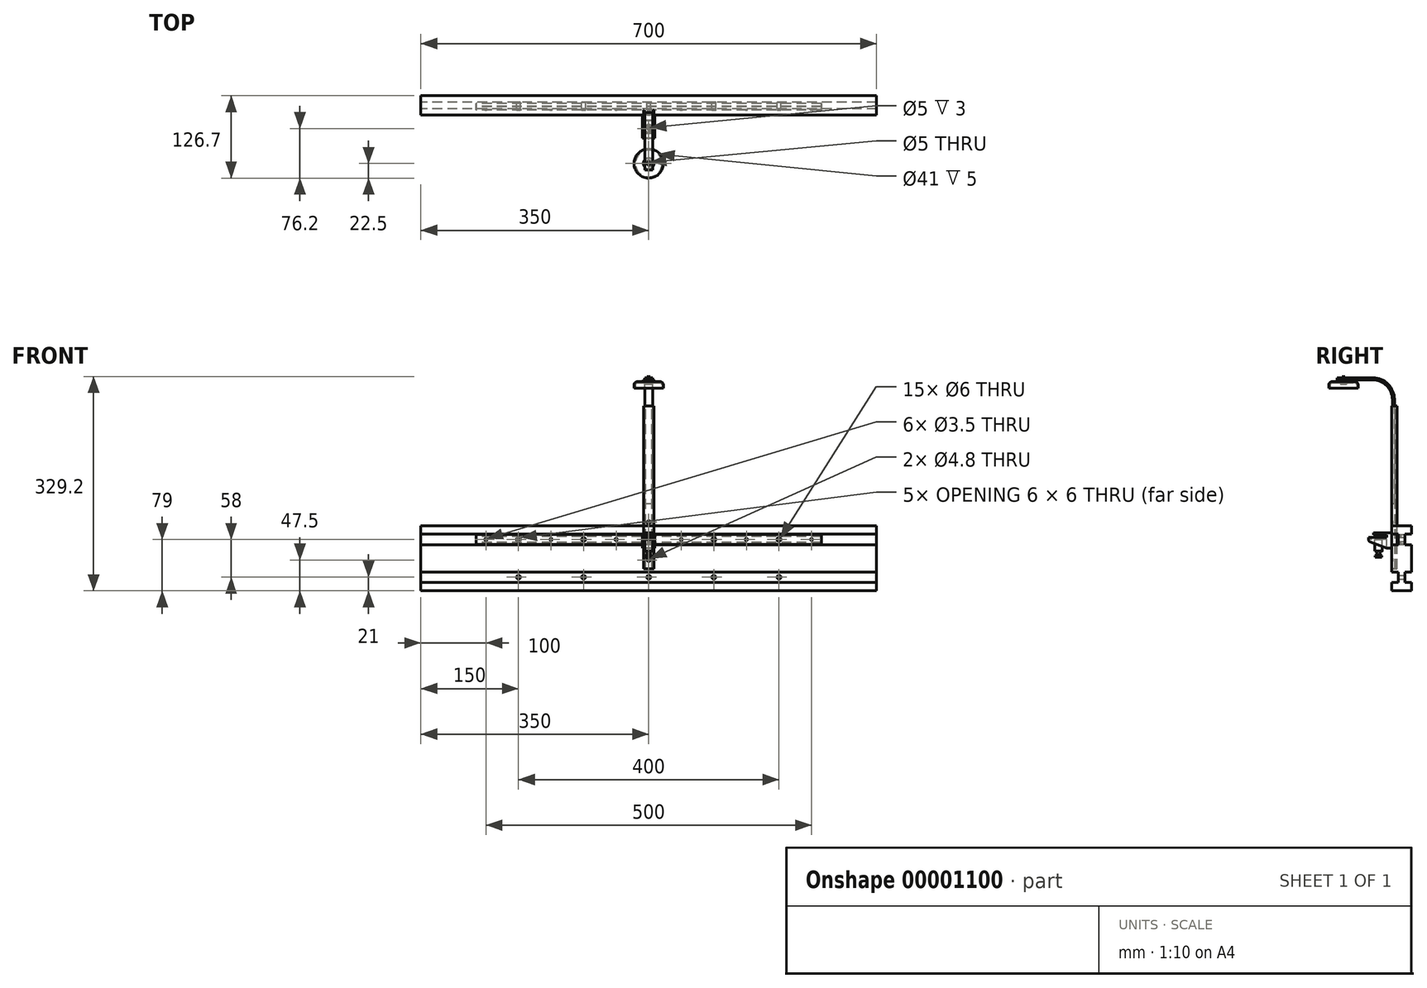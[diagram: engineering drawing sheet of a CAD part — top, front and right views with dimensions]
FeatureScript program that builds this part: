
annotation { "Feature Type Name" : "Feature", "Feature Type Description" : "" }
export const myFeature = defineFeature(function(context is Context, id is Id, definition is map)
    precondition{}
    {
        {
            var Q0;
            Q0=qCreatedBy(makeId("Right.planeOp"),FACE);
            var sketch = newSketch(context, id + "F0", { "sketchPlane" : qUnion([Q0])});
            skLineSegment(sketch, "E0", {"start": v(0, 10) * mm, "end": v(-28, 10) * mm});
            skLineSegment(sketch, "E1", {"start": v(-28, 10) * mm, "end": v(-28, 7) * mm});
            skLineSegment(sketch, "E2", {"start": v(-28, 7) * mm, "end": v(-8, 7) * mm});
            skLineSegment(sketch, "E3", {"start": v(-8, 7) * mm, "end": v(-8, 3) * mm});
            skLineSegment(sketch, "E4", {"start": v(-8, 3) * mm, "end": v(-35.5, 3) * mm});
            skLineSegment(sketch, "E5", {"start": v(-35.5, 3) * mm, "end": v(-35.5, -0.9) * mm});
            skLineSegment(sketch, "E6", {"start": v(-33.53, -3.72) * mm, "end": v(-8, -13) * mm});
            skLineSegment(sketch, "E7", {"start": v(-8, -13) * mm, "end": v(0, -13) * mm});
            skLineSegment(sketch, "E8", {"start": v(0, -13) * mm, "end": v(0, 10) * mm});
            skLineSegment(sketch, "E9", {"start": v(-8, 0) * mm, "end": v(-35.5, 0) * mm});
            skLineSegment(sketch, "E10", {"start": v(-8, -13) * mm, "end": v(-8, 0) * mm});
            skPoint(sketch, "E11.visualSharp", {"position": v(-35.5, -3) * mm});
            skArc(sketch, "E11.filletArc", {"start": v(-35.5, -0.9) * mm, "mid": v(-34.96, -2.62) * mm, "end": v(-33.53, -3.72) * mm});
            skSolve(sketch);
        }
        {
            var Q0;
            Q0 = qSketchRegion(id + "F0", true);
            extrude(context, id + "F1", {"entities" : qUnion([Q0]), "depth" : 19 * mm, "symmetric" : true});
        }
        {
            var Q0;
            {var subQ0=sQuery(id+"F0.wireOp",EDGE,"E6");Q0=makeQuery(id+"F0.imprint","IMPRINT",FACE,{"disambiguationData":[TD([[makeQuery(id+"F0.imprint","IMPRINT",EDGE,{"derivedFrom":subQ0}),1.0]])]});}
            extrude(context, id + "F2", {"entities" : qUnion([Q0]), "operationType" : NewBodyOperationType.REMOVE, "oppositeDirection" : true, "depth" : 15 * mm, "symmetric" : true});
        }
        {
            var Q0;
            Q0=qCreatedBy(makeId("Right.planeOp"),FACE);
            var sketch = newSketch(context, id + "F3", { "sketchPlane" : qUnion([Q0])});
            skLineSegment(sketch, "E12", {"start": v(-20.5, 6) * mm, "end": v(-20.5, -27) * mm});
            skLineSegment(sketch, "E13", {"start": v(-20.5, -27) * mm, "end": v(-15.5, -27) * mm});
            skLineSegment(sketch, "E14", {"start": v(-15.5, -27) * mm, "end": v(-15.5, -25) * mm});
            skLineSegment(sketch, "E15", {"start": v(-15.5, -25) * mm, "end": v(-18.25, -23.5) * mm});
            skLineSegment(sketch, "E16", {"start": v(-18.25, -23.5) * mm, "end": v(-18.25, -18) * mm});
            skLineSegment(sketch, "E17", {"start": v(-18.25, 6) * mm, "end": v(-20.5, 6) * mm});
            skLineSegment(sketch, "E18", {"start": v(-18.25, -18) * mm, "end": v(-14.5, -18) * mm});
            skLineSegment(sketch, "E19", {"start": v(-14.5, -18) * mm, "end": v(-14.5, 0) * mm});
            skLineSegment(sketch, "E20", {"start": v(-14.5, 0) * mm, "end": v(-18.25, 0) * mm});
            skLineSegment(sketch, "E21", {"start": v(-18, 0) * mm, "end": v(-18, 3) * mm});
            skLineSegment(sketch, "E22", {"start": v(-18, 3) * mm, "end": v(-18.25, 3) * mm});
            skLineSegment(sketch, "E23.trimOffspring", {"start": v(-18.25, 0) * mm, "end": v(-18.25, 6) * mm});
            skSolve(sketch);
        }
        {
            var Q0;
            {var subQ5=sQuery(id+"F3.wireOp",EDGE,"E21");Q0=makeQuery(id+"F3.imprint","IMPRINT",FACE,{"disambiguationData":[TD([[makeQuery(id+"F3.imprint","IMPRINT",EDGE,{"derivedFrom":subQ5}),1.0]])]});}
            var Q1;
            Q1=sQuery(id+"F3.wireOp",EDGE,"E12");
            revolve(context, id + "F4", {"operationType" : NewBodyOperationType.REMOVE, "entities" : qUnion([Q0]), "axis" : qUnion([Q1]), "revolveType" : RevolveType.FULL, "oppositeDirection" : true});
        }
        {
            var Q0;
            Q0=makeQuery(id+"F3.imprint","IMPRINT",FACE,{"disambiguationData":[TD([[makeQuery(id+"F3.imprint","IMPRINT",EDGE,{"derivedFrom":sQuery(id+"F3.wireOp",EDGE,"E12")}),1.0]])]});
            var Q1;
            Q1=sQuery(id+"F3.wireOp",EDGE,"E12");
            revolve(context, id + "F5", {"operationType" : NewBodyOperationType.ADD, "entities" : qUnion([Q0]), "axis" : qUnion([Q1]), "revolveType" : RevolveType.FULL});
        }
        {
            var Q0;
            Q0=makeQuery(id+"F5.opRevolve","SWEPT_EDGE",EDGE,{"disambiguationData":[OSD([sQuery(id+"F3.wireOp",EDGE,"E17"),sQuery(id+"F3.wireOp",EDGE,"E23.trimOffspring")])]});
            chamfer(context, id + "F6", {"entities" : qUnion([Q0]), "width" : .5 * mm, "tangentPropagation" : true});
        }
        {
            var Q0;
            Q0=qCreatedBy(makeId("Top.planeOp"),FACE);
            var sketch = newSketch(context, id + "F7", { "sketchPlane" : qUnion([Q0])});
            skLineSegment(sketch, "E24", {"start": v(0, 0) * mm, "end": v(-7.75, 0) * mm});
            skLineSegment(sketch, "E25", {"start": v(-7.75, 0) * mm, "end": v(-7.75, 7.8) * mm});
            skLineSegment(sketch, "E26", {"start": v(-7.75, 7.8) * mm, "end": v(-6.95, 7.8) * mm});
            skLineSegment(sketch, "E27", {"start": v(-6.95, 7.8) * mm, "end": v(-6.95, 6) * mm});
            skLineSegment(sketch, "E28", {"start": v(-6.95, 6) * mm, "end": v(-4.7, 6) * mm});
            skLineSegment(sketch, "E29", {"start": v(-4.7, 6) * mm, "end": v(-4.7, 5.2) * mm});
            skLineSegment(sketch, "E30", {"start": v(-4.7, 5.2) * mm, "end": v(-6.95, 5.2) * mm});
            skLineSegment(sketch, "E31", {"start": v(-6.95, 5.2) * mm, "end": v(-6.95, 0.8) * mm});
            skLineSegment(sketch, "E32", {"start": v(-6.95, 0.8) * mm, "end": v(0, 0.8) * mm});
            skLineSegment(sketch, "E33", {"start": v(0, 0.8) * mm, "end": v(0, 0) * mm, "construction": true});
            skLineSegment(sketch, "E34.MirrorCS", {"start": v(6.95, 0.8) * mm, "end": v(0, 0.8) * mm});
            skLineSegment(sketch, "E35.MirrorCS", {"start": v(6.95, 5.2) * mm, "end": v(6.95, 0.8) * mm});
            skLineSegment(sketch, "E36.MirrorCS", {"start": v(4.7, 5.2) * mm, "end": v(6.95, 5.2) * mm});
            skLineSegment(sketch, "E37.MirrorCS", {"start": v(4.7, 6) * mm, "end": v(4.7, 5.2) * mm});
            skLineSegment(sketch, "E38.MirrorCS", {"start": v(6.95, 6) * mm, "end": v(4.7, 6) * mm});
            skLineSegment(sketch, "E39.MirrorCS", {"start": v(6.95, 7.8) * mm, "end": v(6.95, 6) * mm});
            skLineSegment(sketch, "E40.MirrorCS", {"start": v(7.75, 7.8) * mm, "end": v(6.95, 7.8) * mm});
            skLineSegment(sketch, "E41.MirrorCS", {"start": v(7.75, 0) * mm, "end": v(7.75, 7.8) * mm});
            skLineSegment(sketch, "E42.MirrorCS", {"start": v(0, 0) * mm, "end": v(7.75, 0) * mm});
            skSolve(sketch);
        }
        {
            var Q0;
            Q0 = qSketchRegion(id + "F7", true);
            extrude(context, id + "F8", {"entities" : qUnion([Q0]), "operationType" : NewBodyOperationType.ADD, "oppositeDirection" : true, "depth" : (13 + 32) * mm, "hasSecondDirection" : true, "secondDirectionOppositeDirection" : false, "secondDirectionDepth" : (250 - 45) * mm});
        }
        {
            var Q0;
            Q0=qCreatedBy(makeId("Front.planeOp"),FACE);
            var sketch = newSketch(context, id + "F9", { "sketchPlane" : qUnion([Q0])});
            skPoint(sketch, "E43", {"position": v(0, 26.5) * mm});
            skPoint(sketch, "E44", {"position": v(0, -31.5) * mm});
            skSolve(sketch);
        }
        {
            var Q0;
            Q0=sQuery(id+"F9.wireOp",VERTEX,"E43");
            var Q1;
            Q1=sQuery(id+"F9.wireOp",VERTEX,"E44");
            var Q2;
            Q2=makeQuery(id+"F4.boolean.opBoolean","SPLIT",BODY,{"disambiguationData":[OD(0.0)],"derivedFrom":makeQuery(id+"F1.opExtrude","SWEPT_BODY",BODY,{"disambiguationData":[OSD([sQuery(id+"F0.wireOp",EDGE,"E0"),sQuery(id+"F0.wireOp",EDGE,"E1"),sQuery(id+"F0.wireOp",EDGE,"E2"),sQuery(id+"F0.wireOp",EDGE,"E3"),sQuery(id+"F0.wireOp",EDGE,"E4"),sQuery(id+"F0.wireOp",EDGE,"E5"),sQuery(id+"F0.wireOp",EDGE,"E6"),sQuery(id+"F0.wireOp",EDGE,"E7"),sQuery(id+"F0.wireOp",EDGE,"E8"),sQuery(id+"F0.wireOp",EDGE,"E11.filletArc")])]})});
            hole(context, id + "F10", {"style" : HoleStyle.SIMPLE, "endStyle" : HoleEndStyle.THROUGH, "holeDiameter" : 4.8 * mm, "locations" : qUnion([Q0, Q1]), "scope" : qUnion([Q2]), "isTappedThrough" : true});
        }
        {
            var Q0;
            Q0=qCreatedBy(makeId("Right.planeOp"),FACE);
            var sketch = newSketch(context, id + "F11", { "sketchPlane" : qUnion([Q0])});
            skLineSegment(sketch, "E45", {"start": v(0.8, 55) * mm, "end": v(0.8, 215) * mm});
            skArc(sketch, "E46", {"start": v(0.8, 215) * mm, "mid": v(-7.99, 236.21) * mm, "end": v(-29.2, 245) * mm});
            skLineSegment(sketch, "E47", {"start": v(-29.2, 245) * mm, "end": v(-84.2, 245) * mm});
            skSolve(sketch);
        }
        {
            var Q0;
            Q0=sQuery(id+"F11.wireOp",VERTEX,"E45.start");
            var Q1;
            Q1=qCreatedBy(makeId("Top.planeOp"),FACE);
            cPlane(context, id + "F12", {"entities" : qUnion([Q0, Q1]), "cplaneType" : CPlaneType.PLANE_POINT, "offset" : 25 * mm, "width" : 150 * mm, "height" : 150 * mm});
        }
        {
            var Q0;
            Q0=qCreatedBy(id+"F12.planeOp",FACE);
            var sketch = newSketch(context, id + "F13", { "sketchPlane" : qUnion([Q0])});
            skLineSegment(sketch, "E48.bottom", {"start": v(-6.15, 0.8) * mm, "end": v(6.15, 0.8) * mm});
            skLineSegment(sketch, "E48.top", {"start": v(-6.15, 4) * mm, "end": v(6.15, 4) * mm});
            skLineSegment(sketch, "E48.left", {"start": v(-6.15, 0.8) * mm, "end": v(-6.15, 4) * mm});
            skLineSegment(sketch, "E48.right", {"start": v(6.15, 0.8) * mm, "end": v(6.15, 4) * mm});
            skPoint(sketch, "E49", {"position": v(0, 0.8) * mm});
            skSolve(sketch);
        }
        {
            var Q0;
            Q0 = qSketchRegion(id + "F13", true);
            var Q1;
            Q1 = qConstructionFilter(qBodyType(qCreatedBy(id + "F11" ,EDGE), BodyType.WIRE), ConstructionObject.NO);
            sweep(context, id + "F14", {"profiles" : qUnion([Q0]), "path" : qUnion([Q1])});
        }
        {
            var Q0;
            Q0=qCreatedBy(makeId("Right.planeOp"),FACE);
            var sketch = newSketch(context, id + "F15", { "sketchPlane" : qUnion([Q0])});
            skLineSegment(sketch, "E50", {"start": v(-74.2, 250.2) * mm, "end": v(-71.7, 250.2) * mm});
            skLineSegment(sketch, "E51", {"start": v(-71.7, 250.2) * mm, "end": v(-71.7, 240.5) * mm});
            skLineSegment(sketch, "E52", {"start": v(-69.2, 240.5) * mm, "end": v(-69.2, 238.5) * mm});
            skLineSegment(sketch, "E53", {"start": v(-69.2, 238.5) * mm, "end": v(-74.2, 238.5) * mm});
            skLineSegment(sketch, "E54", {"start": v(-74.2, 238.5) * mm, "end": v(-74.2, 250.2) * mm});
            skLineSegment(sketch, "E55", {"start": v(-71.7, 245) * mm, "end": v(-65.95, 245) * mm});
            skLineSegment(sketch, "E56", {"start": v(-65.95, 245) * mm, "end": v(-65.95, 242.5) * mm});
            skLineSegment(sketch, "E57", {"start": v(-65.95, 242.5) * mm, "end": v(-56.7, 242.5) * mm});
            skLineSegment(sketch, "E58", {"start": v(-51.7, 237.5) * mm, "end": v(-51.7, 232.5) * mm});
            skLineSegment(sketch, "E59", {"start": v(-51.7, 232.5) * mm, "end": v(-53.7, 232.5) * mm});
            skLineSegment(sketch, "E60", {"start": v(-53.7, 232.5) * mm, "end": v(-53.7, 237.5) * mm});
            skLineSegment(sketch, "E61", {"start": v(-56.7, 240.5) * mm, "end": v(-71.7, 240.5) * mm});
            skPoint(sketch, "E62.visualSharp", {"position": v(-51.7, 242.5) * mm});
            skArc(sketch, "E62.filletArc", {"start": v(-51.7, 237.5) * mm, "mid": v(-53.16, 241.04) * mm, "end": v(-56.7, 242.5) * mm});
            skPoint(sketch, "E63.visualSharp", {"position": v(-53.7, 240.5) * mm});
            skArc(sketch, "E63.filletArc", {"start": v(-53.7, 237.5) * mm, "mid": v(-54.58, 239.62) * mm, "end": v(-56.7, 240.5) * mm});
            skLineSegment(sketch, "E64", {"start": v(-56.7, 240.5) * mm, "end": v(-56.7, 242.5) * mm, "construction": true});
            skLineSegment(sketch, "E65", {"start": v(-54.58, 239.62) * mm, "end": v(-53.16, 241.04) * mm, "construction": true});
            skSolve(sketch);
        }
        {
            var Q0;
            {var subQ5=sQuery(id+"F15.wireOp",EDGE,"E50");Q0=makeQuery(id+"F15.imprint","IMPRINT",FACE,{"disambiguationData":[TD([[makeQuery(id+"F15.imprint","IMPRINT",EDGE,{"derivedFrom":subQ5}),-1.0]])]});}
            var Q1;
            Q1=sQuery(id+"F15.wireOp",EDGE,"E54");
            revolve(context, id + "F16", {"operationType" : NewBodyOperationType.ADD, "entities" : qUnion([Q0]), "axis" : qUnion([Q1]), "revolveType" : RevolveType.FULL});
        }
        {
            var Q0;
            {var subQ0=sQuery(id+"F15.wireOp",EDGE,"E55");Q0=makeQuery(id+"F15.imprint","IMPRINT",FACE,{"disambiguationData":[TD([[makeQuery(id+"F15.imprint","IMPRINT",EDGE,{"derivedFrom":subQ0}),-1.0]])]});}
            var Q1;
            Q1=sQuery(id+"F15.wireOp",EDGE,"E54");
            revolve(context, id + "F17", {"entities" : qUnion([Q0]), "axis" : qUnion([Q1]), "revolveType" : RevolveType.FULL});
        }
        {
            var Q0;
            Q0=qCreatedBy(makeId("Right.planeOp"),FACE);
            var sketch = newSketch(context, id + "F18", { "sketchPlane" : qUnion([Q0])});
            skLineSegment(sketch, "E66", {"start": v(7.8, 0) * mm, "end": v(7.8, 7.75) * mm});
            skLineSegment(sketch, "E67", {"start": v(7.8, 7.75) * mm, "end": v(18.3, 7.75) * mm});
            skLineSegment(sketch, "E68", {"start": v(18.3, 7.75) * mm, "end": v(18.3, 6.95) * mm});
            skLineSegment(sketch, "E69", {"start": v(18.3, 6.95) * mm, "end": v(13.8, 6.95) * mm});
            skLineSegment(sketch, "E70", {"start": v(13.8, 6.95) * mm, "end": v(13.8, 4.7) * mm});
            skLineSegment(sketch, "E71", {"start": v(13.8, 4.7) * mm, "end": v(13, 4.7) * mm});
            skLineSegment(sketch, "E72", {"start": v(13, 4.7) * mm, "end": v(13, 6.95) * mm});
            skLineSegment(sketch, "E73", {"start": v(13, 6.95) * mm, "end": v(8.6, 6.95) * mm});
            skLineSegment(sketch, "E74", {"start": v(8.6, 6.95) * mm, "end": v(8.6, 0) * mm});
            skLineSegment(sketch, "E75", {"start": v(8.6, 0) * mm, "end": v(7.8, 0) * mm, "construction": true});
            skLineSegment(sketch, "E76.MirrorCS", {"start": v(18.3, -6.95) * mm, "end": v(13.8, -6.95) * mm});
            skLineSegment(sketch, "E77.MirrorCS", {"start": v(18.3, -7.75) * mm, "end": v(18.3, -6.95) * mm});
            skLineSegment(sketch, "E78.MirrorCS", {"start": v(13.8, -6.95) * mm, "end": v(13.8, -4.7) * mm});
            skLineSegment(sketch, "E79.MirrorCS", {"start": v(13.8, -4.7) * mm, "end": v(13, -4.7) * mm});
            skLineSegment(sketch, "E80.MirrorCS", {"start": v(13, -4.7) * mm, "end": v(13, -6.95) * mm});
            skLineSegment(sketch, "E81.MirrorCS", {"start": v(13, -6.95) * mm, "end": v(8.6, -6.95) * mm});
            skLineSegment(sketch, "E82.MirrorCS", {"start": v(8.6, -6.95) * mm, "end": v(8.6, 0) * mm});
            skLineSegment(sketch, "E83.MirrorCS", {"start": v(7.8, 0) * mm, "end": v(7.8, -7.75) * mm});
            skLineSegment(sketch, "E84.MirrorCS", {"start": v(7.8, -7.75) * mm, "end": v(18.3, -7.75) * mm});
            skSolve(sketch);
        }
        {
            var Q0;
            Q0 = qSketchRegion(id + "F18", true);
            extrude(context, id + "F19", {"entities" : qUnion([Q0]), "depth" : 530 * mm, "symmetric" : true});
        }
        {
            var Q0;
            Q0=makeQuery(id+"F19.opExtrude","SWEPT_FACE",FACE,{"disambiguationData":[OSD([sQuery(id+"F18.wireOp",EDGE,"E66"),sQuery(id+"F18.wireOp",EDGE,"E83.MirrorCS")])]});
            var sketch = newSketch(context, id + "F20", { "sketchPlane" : qUnion([Q0])});
            skPoint(sketch, "E85", {"position": v(-250, 0) * mm});
            skPoint(sketch, "E86.1.0.0", {"position": v(-150, 0) * mm});
            skPoint(sketch, "E86.2.0.0", {"position": v(-50, 0) * mm});
            skPoint(sketch, "E86.3.0.0", {"position": v(50, 0) * mm});
            skPoint(sketch, "E86.4.0.0", {"position": v(150, 0) * mm});
            skPoint(sketch, "E86.5.0.0", {"position": v(250, 0) * mm});
            skLineSegment(sketch, "E86.direction1", {"start": v(-250, 0) * mm, "end": v(-150, 0) * mm, "construction": true});
            skLineSegment(sketch, "E87", {"start": v(0, 7.75) * mm, "end": v(0, -7.75) * mm, "construction": true});
            skPoint(sketch, "E88", {"position": v(-200, 0) * mm});
            skPoint(sketch, "E89.1.0.0", {"position": v(-100, 0) * mm});
            skPoint(sketch, "E89.2.0.0", {"position": v(0, 0) * mm});
            skPoint(sketch, "E89.3.0.0", {"position": v(100, 0) * mm});
            skPoint(sketch, "E89.4.0.0", {"position": v(200, 0) * mm});
            skLineSegment(sketch, "E89.direction1", {"start": v(-200, 0) * mm, "end": v(-100, 0) * mm, "construction": true});
            skSolve(sketch);
        }
        {
            var Q0;
            Q0=sQuery(id+"F20.wireOp",VERTEX,"E85");
            var Q1;
            Q1=sQuery(id+"F20.wireOp",VERTEX,"E86.1.0.0");
            var Q2;
            Q2=sQuery(id+"F20.wireOp",VERTEX,"E86.2.0.0");
            var Q3;
            Q3=sQuery(id+"F20.wireOp",VERTEX,"E86.3.0.0");
            var Q4;
            Q4=sQuery(id+"F20.wireOp",VERTEX,"E86.4.0.0");
            var Q5;
            Q5=sQuery(id+"F20.wireOp",VERTEX,"E86.5.0.0");
            var Q6;
            Q6=makeQuery(id+"F19.opExtrude","SWEPT_BODY",BODY,{"disambiguationData":[OSD([sQuery(id+"F18.wireOp",EDGE,"E66"),sQuery(id+"F18.wireOp",EDGE,"E67"),sQuery(id+"F18.wireOp",EDGE,"E68"),sQuery(id+"F18.wireOp",EDGE,"E69"),sQuery(id+"F18.wireOp",EDGE,"E70"),sQuery(id+"F18.wireOp",EDGE,"E71"),sQuery(id+"F18.wireOp",EDGE,"E72"),sQuery(id+"F18.wireOp",EDGE,"E73"),sQuery(id+"F18.wireOp",EDGE,"E74"),sQuery(id+"F18.wireOp",EDGE,"E76.MirrorCS"),sQuery(id+"F18.wireOp",EDGE,"E77.MirrorCS"),sQuery(id+"F18.wireOp",EDGE,"E78.MirrorCS"),sQuery(id+"F18.wireOp",EDGE,"E79.MirrorCS"),sQuery(id+"F18.wireOp",EDGE,"E80.MirrorCS"),sQuery(id+"F18.wireOp",EDGE,"E81.MirrorCS"),sQuery(id+"F18.wireOp",EDGE,"E82.MirrorCS"),sQuery(id+"F18.wireOp",EDGE,"E83.MirrorCS"),sQuery(id+"F18.wireOp",EDGE,"E84.MirrorCS")])]});
            hole(context, id + "F21", {"style" : HoleStyle.SIMPLE, "endStyle" : HoleEndStyle.THROUGH, "holeDiameter" : 3.5 * mm, "locations" : qUnion([Q0, Q1, Q2, Q3, Q4, Q5]), "scope" : qUnion([Q6]), "isTappedThrough" : true});
        }
        {
            var Q0;
            Q0=sQuery(id+"F20.wireOp",VERTEX,"E88");
            var Q1;
            Q1=sQuery(id+"F20.wireOp",VERTEX,"E89.1.0.0");
            var Q2;
            Q2=sQuery(id+"F20.wireOp",VERTEX,"E89.2.0.0");
            var Q3;
            Q3=sQuery(id+"F20.wireOp",VERTEX,"E89.3.0.0");
            var Q4;
            Q4=sQuery(id+"F20.wireOp",VERTEX,"E89.4.0.0");
            var Q5;
            Q5=makeQuery(id+"F19.opExtrude","SWEPT_BODY",BODY,{"disambiguationData":[OSD([sQuery(id+"F18.wireOp",EDGE,"E66"),sQuery(id+"F18.wireOp",EDGE,"E67"),sQuery(id+"F18.wireOp",EDGE,"E68"),sQuery(id+"F18.wireOp",EDGE,"E69"),sQuery(id+"F18.wireOp",EDGE,"E70"),sQuery(id+"F18.wireOp",EDGE,"E71"),sQuery(id+"F18.wireOp",EDGE,"E72"),sQuery(id+"F18.wireOp",EDGE,"E73"),sQuery(id+"F18.wireOp",EDGE,"E74"),sQuery(id+"F18.wireOp",EDGE,"E76.MirrorCS"),sQuery(id+"F18.wireOp",EDGE,"E77.MirrorCS"),sQuery(id+"F18.wireOp",EDGE,"E78.MirrorCS"),sQuery(id+"F18.wireOp",EDGE,"E79.MirrorCS"),sQuery(id+"F18.wireOp",EDGE,"E80.MirrorCS"),sQuery(id+"F18.wireOp",EDGE,"E81.MirrorCS"),sQuery(id+"F18.wireOp",EDGE,"E82.MirrorCS"),sQuery(id+"F18.wireOp",EDGE,"E83.MirrorCS"),sQuery(id+"F18.wireOp",EDGE,"E84.MirrorCS")])]});
            hole(context, id + "F22", {"style" : HoleStyle.SIMPLE, "endStyle" : HoleEndStyle.THROUGH, "holeDiameter" : 6 * mm, "locations" : qUnion([Q0, Q1, Q2, Q3, Q4]), "scope" : qUnion([Q5]), "isTappedThrough" : true});
        }
        {
            var Q0;
            Q0=qCreatedBy(makeId("Right.planeOp"),FACE);
            var sketch = newSketch(context, id + "F23", { "sketchPlane" : qUnion([Q0])});
            skLineSegment(sketch, "E90", {"start": v(0, 21) * mm, "end": v(0, 8) * mm});
            skLineSegment(sketch, "E91", {"start": v(0, -50) * mm, "end": v(10, -50) * mm});
            skLineSegment(sketch, "E92", {"start": v(10, -50) * mm, "end": v(10, -66) * mm});
            skLineSegment(sketch, "E93", {"start": v(10, -66) * mm, "end": v(0, -66) * mm});
            skLineSegment(sketch, "E94", {"start": v(0, -66) * mm, "end": v(0, -79) * mm});
            skLineSegment(sketch, "E95", {"start": v(0, -79) * mm, "end": v(15, -79) * mm});
            skLineSegment(sketch, "E96", {"start": v(15, -79) * mm, "end": v(15, 21) * mm, "construction": true});
            skLineSegment(sketch, "E97", {"start": v(15, 21) * mm, "end": v(0, 21) * mm});
            skLineSegment(sketch, "E98", {"start": v(0, -8) * mm, "end": v(10, -8) * mm});
            skLineSegment(sketch, "E99", {"start": v(10, -8) * mm, "end": v(10, 8) * mm});
            skLineSegment(sketch, "E100", {"start": v(10, 8) * mm, "end": v(0, 8) * mm});
            skLineSegment(sketch, "E101.trimOffspring", {"start": v(0, -8) * mm, "end": v(0, -50) * mm});
            skLineSegment(sketch, "E102", {"start": v(10, 0) * mm, "end": v(0, 0) * mm, "construction": true});
            skLineSegment(sketch, "E103", {"start": v(10, -58) * mm, "end": v(0, -58) * mm, "construction": true});
            skLineSegment(sketch, "E104.MirrorCS", {"start": v(15, 21) * mm, "end": v(30, 21) * mm});
            skLineSegment(sketch, "E105.MirrorCS", {"start": v(30, -50) * mm, "end": v(20, -50) * mm});
            skLineSegment(sketch, "E106.MirrorCS", {"start": v(20, -8) * mm, "end": v(20, 8) * mm});
            skLineSegment(sketch, "E107.MirrorCS", {"start": v(30, 21) * mm, "end": v(30, 8) * mm});
            skLineSegment(sketch, "E108.MirrorCS", {"start": v(20, -58) * mm, "end": v(30, -58) * mm, "construction": true});
            skLineSegment(sketch, "E109.MirrorCS", {"start": v(20, 0) * mm, "end": v(30, 0) * mm, "construction": true});
            skLineSegment(sketch, "E110.MirrorCS", {"start": v(30, -66) * mm, "end": v(30, -79) * mm});
            skLineSegment(sketch, "E111.MirrorCS", {"start": v(20, -50) * mm, "end": v(20, -66) * mm});
            skLineSegment(sketch, "E112.MirrorCS", {"start": v(30, -8) * mm, "end": v(30, -50) * mm});
            skLineSegment(sketch, "E113.MirrorCS", {"start": v(30, -8) * mm, "end": v(20, -8) * mm});
            skLineSegment(sketch, "E114.MirrorCS", {"start": v(20, 8) * mm, "end": v(30, 8) * mm});
            skLineSegment(sketch, "E115.MirrorCS", {"start": v(30, -79) * mm, "end": v(15, -79) * mm});
            skLineSegment(sketch, "E116.MirrorCS", {"start": v(20, -66) * mm, "end": v(30, -66) * mm});
            skSolve(sketch);
        }
        {
            var Q0;
            Q0=makeQuery(id+"F23.imprint","IMPRINT",FACE,{"disambiguationData":[TD([[makeQuery(id+"F23.imprint","IMPRINT",EDGE,{"derivedFrom":sQuery(id+"F23.wireOp",EDGE,"E90")}),1.0]])]});
            extrude(context, id + "F24", {"entities" : qUnion([Q0]), "depth" : 700 * mm, "symmetric" : true});
        }
        {
            var Q0;
            Q0=qCreatedBy(makeId("Front.planeOp"),FACE);
            var sketch = newSketch(context, id + "F25", { "sketchPlane" : qUnion([Q0])});
            skLineSegment(sketch, "E117", {"start": v(-200, 0) * mm, "end": v(-200, -58) * mm, "construction": true});
            skLineSegment(sketch, "E118.1.0.0", {"start": v(-100, 0) * mm, "end": v(-100, -58) * mm, "construction": true});
            skLineSegment(sketch, "E118.2.0.0", {"start": v(0, 0) * mm, "end": v(0, -58) * mm, "construction": true});
            skLineSegment(sketch, "E118.3.0.0", {"start": v(100, 0) * mm, "end": v(100, -58) * mm, "construction": true});
            skLineSegment(sketch, "E118.4.0.0", {"start": v(200, 0) * mm, "end": v(200, -58) * mm, "construction": true});
            skLineSegment(sketch, "E118.direction1", {"start": v(-200, -58) * mm, "end": v(-100, -58) * mm, "construction": true});
            skSolve(sketch);
        }
        {
            var Q0;
            Q0=sQuery(id+"F25.wireOp",VERTEX,"E117.start");
            var Q1;
            Q1=sQuery(id+"F25.wireOp",VERTEX,"E118.1.0.0.start");
            var Q2;
            Q2=sQuery(id+"F25.wireOp",VERTEX,"E118.2.0.0.start");
            var Q3;
            Q3=sQuery(id+"F25.wireOp",VERTEX,"E118.3.0.0.start");
            var Q4;
            Q4=sQuery(id+"F25.wireOp",VERTEX,"E118.4.0.0.start");
            var Q5;
            Q5=sQuery(id+"F25.wireOp",VERTEX,"E118.direction1.start");
            var Q6;
            Q6=sQuery(id+"F25.wireOp",VERTEX,"E118.direction1.end");
            var Q7;
            Q7=sQuery(id+"F25.wireOp",VERTEX,"E118.2.0.0.end");
            var Q8;
            Q8=sQuery(id+"F25.wireOp",VERTEX,"E118.3.0.0.end");
            var Q9;
            Q9=sQuery(id+"F25.wireOp",VERTEX,"E118.4.0.0.end");
            var Q10;
            Q10=makeQuery(id+"F24.opExtrude","SWEPT_BODY",BODY,{"disambiguationData":[OSD([sQuery(id+"F23.wireOp",EDGE,"E90"),sQuery(id+"F23.wireOp",EDGE,"E91"),sQuery(id+"F23.wireOp",EDGE,"E92"),sQuery(id+"F23.wireOp",EDGE,"E93"),sQuery(id+"F23.wireOp",EDGE,"E94"),sQuery(id+"F23.wireOp",EDGE,"E95"),sQuery(id+"F23.wireOp",EDGE,"E97"),sQuery(id+"F23.wireOp",EDGE,"E98"),sQuery(id+"F23.wireOp",EDGE,"E99"),sQuery(id+"F23.wireOp",EDGE,"E100"),sQuery(id+"F23.wireOp",EDGE,"E101.trimOffspring"),sQuery(id+"F23.wireOp",EDGE,"E104.MirrorCS"),sQuery(id+"F23.wireOp",EDGE,"E105.MirrorCS"),sQuery(id+"F23.wireOp",EDGE,"E106.MirrorCS"),sQuery(id+"F23.wireOp",EDGE,"E107.MirrorCS"),sQuery(id+"F23.wireOp",EDGE,"E110.MirrorCS"),sQuery(id+"F23.wireOp",EDGE,"E111.MirrorCS"),sQuery(id+"F23.wireOp",EDGE,"E112.MirrorCS"),sQuery(id+"F23.wireOp",EDGE,"E113.MirrorCS"),sQuery(id+"F23.wireOp",EDGE,"E114.MirrorCS"),sQuery(id+"F23.wireOp",EDGE,"E115.MirrorCS"),sQuery(id+"F23.wireOp",EDGE,"E116.MirrorCS")])]});
            hole(context, id + "F26", {"style" : HoleStyle.SIMPLE, "endStyle" : HoleEndStyle.THROUGH, "holeDiameter" : 6 * mm, "locations" : qUnion([Q0, Q1, Q2, Q3, Q4, Q5, Q6, Q7, Q8, Q9]), "scope" : qUnion([Q10]), "isTappedThrough" : true});
        }
    });
